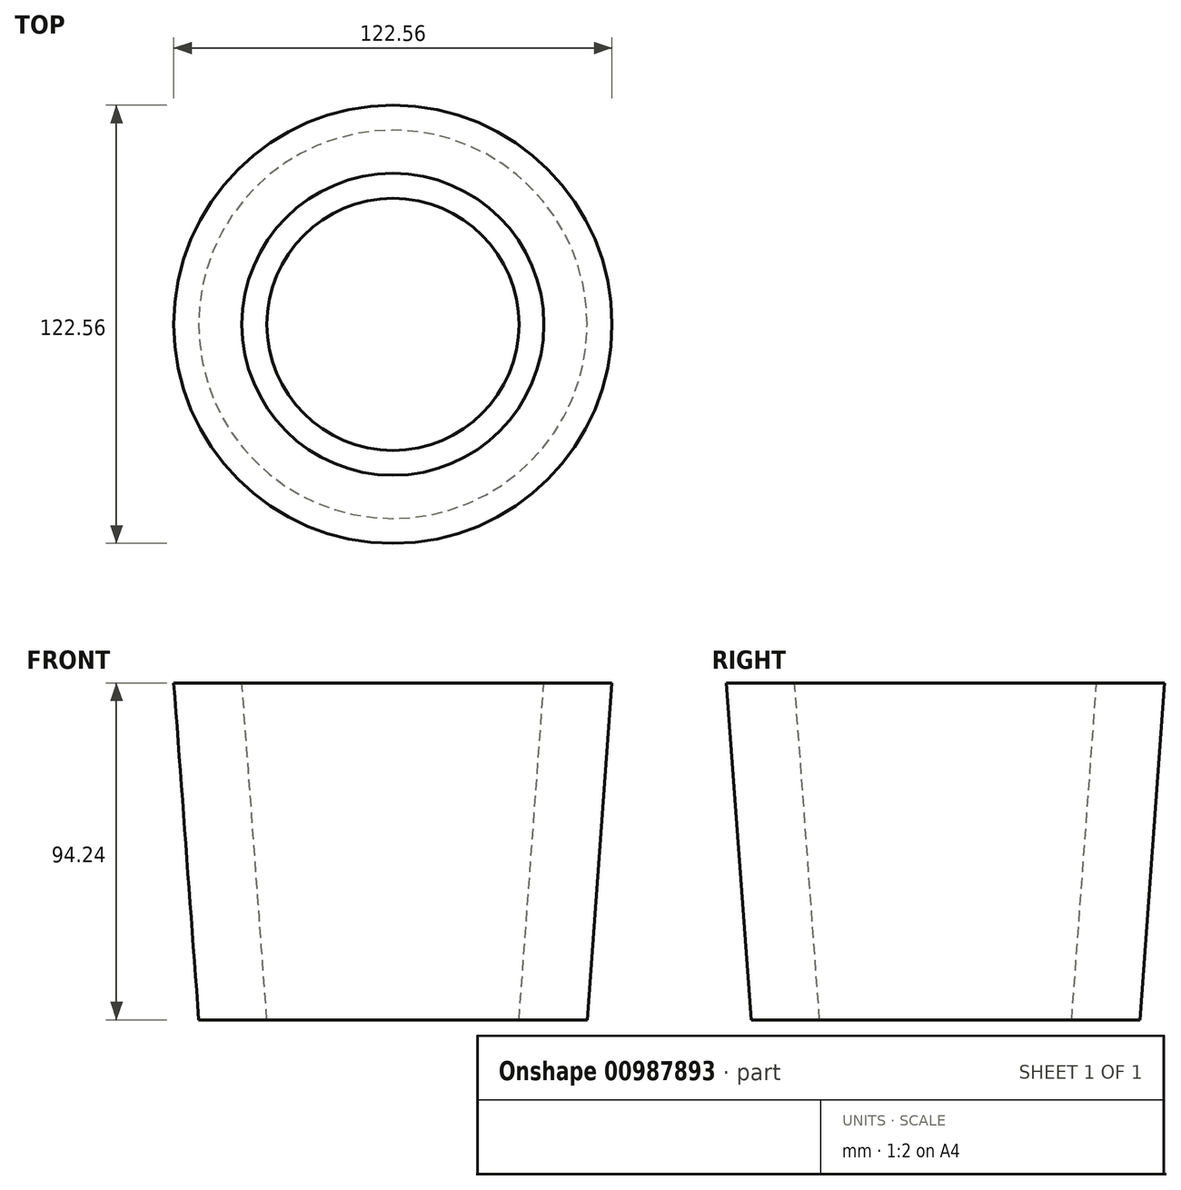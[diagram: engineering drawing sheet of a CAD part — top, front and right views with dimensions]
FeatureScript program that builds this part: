
annotation { "Feature Type Name" : "Feature", "Feature Type Description" : "" }
export const myFeature = defineFeature(function(context is Context, id is Id, definition is map)
    precondition{}
    {
        {
            var Q0;
            Q0=qCreatedBy(makeId("Front.planeOp"),FACE);
            var sketch = newSketch(context, id + "F0", { "sketchPlane" : qUnion([Q0])});
            skLineSegment(sketch, "E0", {"start": v(0, 0) * mm, "end": v(0, 44.65) * mm, "construction": true});
            skLineSegment(sketch, "E1", {"start": v(-42.23, 50.5) * mm, "end": v(-61.28, 50.5) * mm});
            skLineSegment(sketch, "E2", {"start": v(-61.28, 50.5) * mm, "end": v(-54.3, -43.73) * mm});
            skLineSegment(sketch, "E3", {"start": v(-54.3, -43.73) * mm, "end": v(-35.26, -43.73) * mm});
            skLineSegment(sketch, "E4", {"start": v(-42.23, 50.5) * mm, "end": v(-35.26, -43.73) * mm});
            skLineSegment(sketch, "E5", {"start": v(-54.3, -43.73) * mm, "end": v(-54.3, 50.5) * mm, "construction": true});
            skLineSegment(sketch, "E6", {"start": v(-54.3, -43.73) * mm, "end": v(0, -43.73) * mm, "construction": true});
            skLineSegment(sketch, "E7", {"start": v(-61.28, 50.5) * mm, "end": v(0, 50.5) * mm, "construction": true});
            skSolve(sketch);
        }
        {
            var Q0;
            Q0=makeQuery(id+"F0.imprint","IMPRINT",FACE,{"disambiguationData":[TD([[makeQuery(id+"F0.imprint","IMPRINT",EDGE,{"derivedFrom":sQuery(id+"F0.wireOp",EDGE,"E1")}),1.0]])]});
            var Q1;
            Q1=sQuery(id+"F0.wireOp",EDGE,"E0");
            revolve(context, id + "F1", {"surfaceOperationType" : NewSurfaceOperationType.NEW, "entities" : qUnion([Q0]), "axis" : qUnion([Q1]), "revolveType" : RevolveType.FULL});
        }
    });
